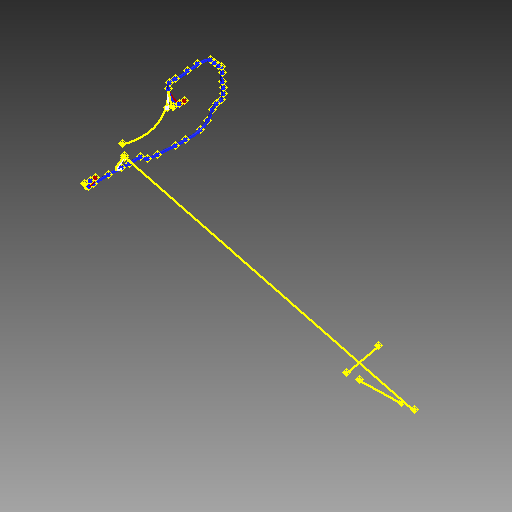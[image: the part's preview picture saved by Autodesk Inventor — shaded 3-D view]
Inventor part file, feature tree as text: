
AUTODESK INVENTOR PART (.ipt)
format: ipt  version: 2017 (Build 210142000, 142)  size: 352,768 bytes
history: native  units: mm (DEFAULTED — no unit token found)
features: other x58, plane x3, sketch x3, sweep x3
ambient origin geometry x8: Origin, YZ Plane, XZ Plane, XY Plane, X Axis, Y Axis, Z Axis, Center Point
bodies: Body1 (feature_tree), Body2 (feature_tree), Body3 (feature_tree)
feature tree (67):
  other  "Work Point1"
  other  "Work Point2"
  other  "Wire1"
  other  "Work Point3"
  other  "Work Point4"
  other  "Wire2"
  other  "Work Point5"
  other  "Work Point6"
  other  "Wire3"
  other  "Work Point7"
  other  "Work Point8"
  other  "Wire4"
  other  "Work Point9"
  other  "Work Point10"
  other  "Wire5"
  other  "Work Point11"
  other  "Work Point12"
  other  "Wire6"
  other  "Work Point13"
  other  "Work Point14"
  other  "Wire7"
  other  "Work Point15"
  other  "Work Point16"
  other  "Wire8"
  other  "Work Point17"
  other  "Work Point18"
  other  "Segment1"
  other  "Work Point19"
  other  "Work Point20"
  plane  "Work Plane1"
  other  "Work Point21"
  other  "Segment2"
  other  "Work Point22"
  other  "Work Point23"
  other  "Work Point24"
  other  "Work Point25"
  other  "Work Point26"
  other  "Work Point27"
  other  "Segment3"
  other  "Work Point28"
  other  "Work Point29"
  other  "Work Point30"
  other  "Work Point31"
  other  "Work Point32"
  other  "Work Point33"
  other  "Work Point34"
  other  "Work Point35"
  other  "Work Point36"
  other  "Work Point37"
  other  "Work Point38"
  other  "Work Point39"
  other  "Work Point40"
  other  "Work Point41"
  other  "Work Point42"
  other  "Work Point43"
  other  "Work Point44"
  plane  "Work Plane2"
  plane  "Work Plane3"
  sketch  "Sketch1"  dims[d0=0.0mm d1=0.0mm d2=0.0mm d3=0.0mm]
  other  "Srf1"
  sketch  "Sketch2"  dims[d4=0.0mm d5=0.0mm]
  other  "Srf2"
  sketch  "Sketch3"
  other  "Srf3"
  sweep  "SweepSrf1"
  sweep  "SweepSrf2"
  sweep  "SweepSrf3"
